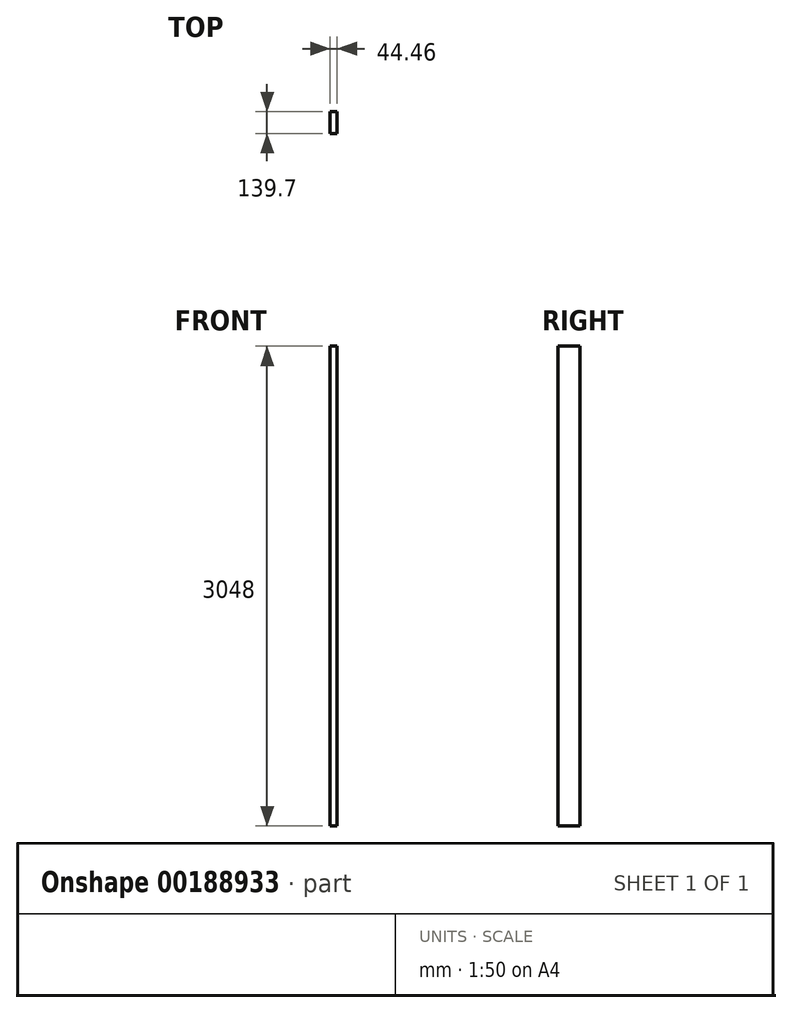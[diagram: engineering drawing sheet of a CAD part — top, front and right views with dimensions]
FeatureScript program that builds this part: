
annotation { "Feature Type Name" : "Feature", "Feature Type Description" : "" }
export const myFeature = defineFeature(function(context is Context, id is Id, definition is map)
    precondition{}
    {
        {
            var Q0;
            Q0=qCreatedBy(makeId("Top.planeOp"),FACE);
            var sketch = newSketch(context, id + "F1", { "sketchPlane" : qUnion([Q0])});
            skLineSegment(sketch, "E0.bottom", {"start": v(22.23, -69.85) * mm, "end": v(-22.22, -69.85) * mm});
            skLineSegment(sketch, "E0.top", {"start": v(22.22, 69.85) * mm, "end": v(-22.23, 69.85) * mm});
            skLineSegment(sketch, "E0.left", {"start": v(22.23, -69.85) * mm, "end": v(22.22, 69.85) * mm});
            skLineSegment(sketch, "E0.right", {"start": v(-22.22, -69.85) * mm, "end": v(-22.23, 69.85) * mm});
            skPoint(sketch, "E0.middle", {"position": v(0, 0) * mm});
            skSolve(sketch);
        }
        {
            var Q0;
            Q0=makeQuery(id+"F1.imprint","IMPRINT",FACE,{"disambiguationData":[TD([[makeQuery(id+"F1.imprint","IMPRINT",EDGE,{"derivedFrom":sQuery(id+"F1.wireOp",EDGE,"E0.bottom")}),-1.0]])]});
            extrude(context, id + "F0", {"entities" : qUnion([Q0]), "endBound" : BoundingType.SYMMETRIC, "depth" : 3048 * mm});
        }
    });
